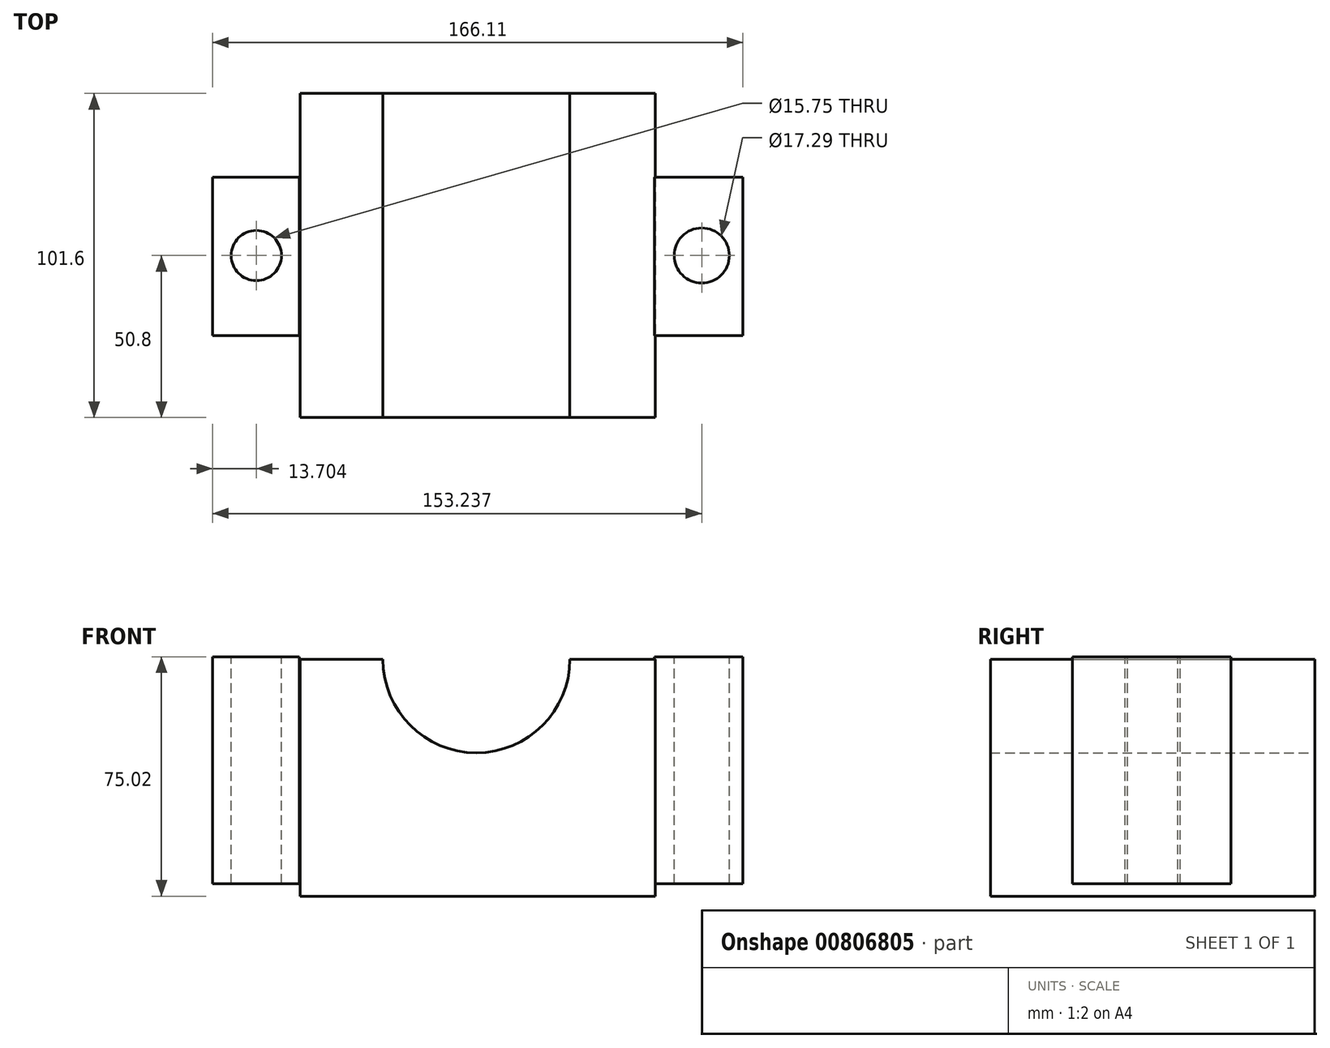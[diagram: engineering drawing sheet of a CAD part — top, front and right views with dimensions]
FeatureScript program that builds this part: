
annotation { "Feature Type Name" : "Feature", "Feature Type Description" : "" }
export const myFeature = defineFeature(function(context is Context, id is Id, definition is map)
    precondition{}
    {
        {
            var Q0;
            Q0=qCreatedBy(makeId("Front.planeOp"),FACE);
            var sketch = newSketch(context, id + "F0", { "sketchPlane" : qUnion([Q0])});
            skLineSegment(sketch, "E0.bottom", {"start": v(-55.23, 34.74) * mm, "end": v(56.06, 34.74) * mm});
            skLineSegment(sketch, "E0.top", {"start": v(-55.23, -39.46) * mm, "end": v(56.06, -39.46) * mm});
            skLineSegment(sketch, "E0.left", {"start": v(-55.23, 34.74) * mm, "end": v(-55.23, -39.46) * mm});
            skLineSegment(sketch, "E0.right", {"start": v(56.06, 34.74) * mm, "end": v(56.06, -39.46) * mm});
            skArc(sketch, "E1", {"start": v(-29.27, 34.74) * mm, "mid": v(0, 5.47) * mm, "end": v(29.27, 34.74) * mm});
            skArc(sketch, "E2", {"start": v(-16.65, 34.74) * mm, "mid": v(0, 18.1) * mm, "end": v(16.65, 34.74) * mm});
            skSolve(sketch);
        }
        {
            var Q0;
            Q0=makeQuery(id+"F0.imprint","IMPRINT",FACE,{"disambiguationData":[TD([[makeQuery(id+"F0.imprint","IMPRINT",EDGE,{"derivedFrom":sQuery(id+"F0.wireOp",EDGE,"E0.top")}),1.0]])]});
            extrude(context, id + "F1", {"entities" : qUnion([Q0]), "endBound" : BoundingType.SYMMETRIC, "depth" : 101.6 * mm, "offsetDistance" : 25.4 * mm});
        }
        {
            var Q0;
            Q0=qCreatedBy(makeId("Top.planeOp"),FACE);
            var sketch = newSketch(context, id + "F2", { "sketchPlane" : qUnion([Q0])});
            skLineSegment(sketch, "E3.bottom", {"start": v(55.79, 24.5) * mm, "end": v(83.47, 24.5) * mm});
            skLineSegment(sketch, "E3.top", {"start": v(55.79, -25.06) * mm, "end": v(83.47, -25.06) * mm});
            skLineSegment(sketch, "E3.left", {"start": v(55.79, 24.5) * mm, "end": v(55.79, -25.06) * mm});
            skLineSegment(sketch, "E3.right", {"start": v(83.47, 24.5) * mm, "end": v(83.47, -25.06) * mm});
            skLineSegment(sketch, "E4.bottom", {"start": v(-55.5, 24.5) * mm, "end": v(-82.64, 24.5) * mm});
            skLineSegment(sketch, "E4.top", {"start": v(-55.5, -25.06) * mm, "end": v(-82.64, -25.06) * mm});
            skLineSegment(sketch, "E4.left", {"start": v(-55.5, 24.5) * mm, "end": v(-55.5, -25.06) * mm});
            skLineSegment(sketch, "E4.right", {"start": v(-82.64, 24.5) * mm, "end": v(-82.64, -25.06) * mm});
            skSolve(sketch);
        }
        {
            var Q0;
            Q0 = qSketchRegion(id + "F2", true);
            extrude(context, id + "F3", {"entities" : qUnion([Q0]), "operationType" : NewBodyOperationType.ADD, "endBound" : BoundingType.SYMMETRIC, "depth" : 71.12 * mm, "offsetDistance" : 25.4 * mm});
        }
        {
            var Q0;
            Q0=qCreatedBy(makeId("Top.planeOp"),FACE);
            var sketch = newSketch(context, id + "F4", { "sketchPlane" : qUnion([Q0])});
            skCircle(sketch, "E5", {"center": v(-68.94, 0) * mm, "radius": 7.87 * mm});
            skCircle(sketch, "E6", {"center": v(70.6, 0) * mm, "radius": 8.65 * mm});
            skSolve(sketch);
        }
        {
            var Q0;
            Q0 = qSketchRegion(id + "F4", true);
            extrude(context, id + "F5", {"entities" : qUnion([Q0]), "operationType" : NewBodyOperationType.REMOVE, "endBound" : BoundingType.SYMMETRIC, "oppositeDirection" : true, "depth" : 101.6 * mm, "offsetDistance" : 25.4 * mm});
        }
    });
